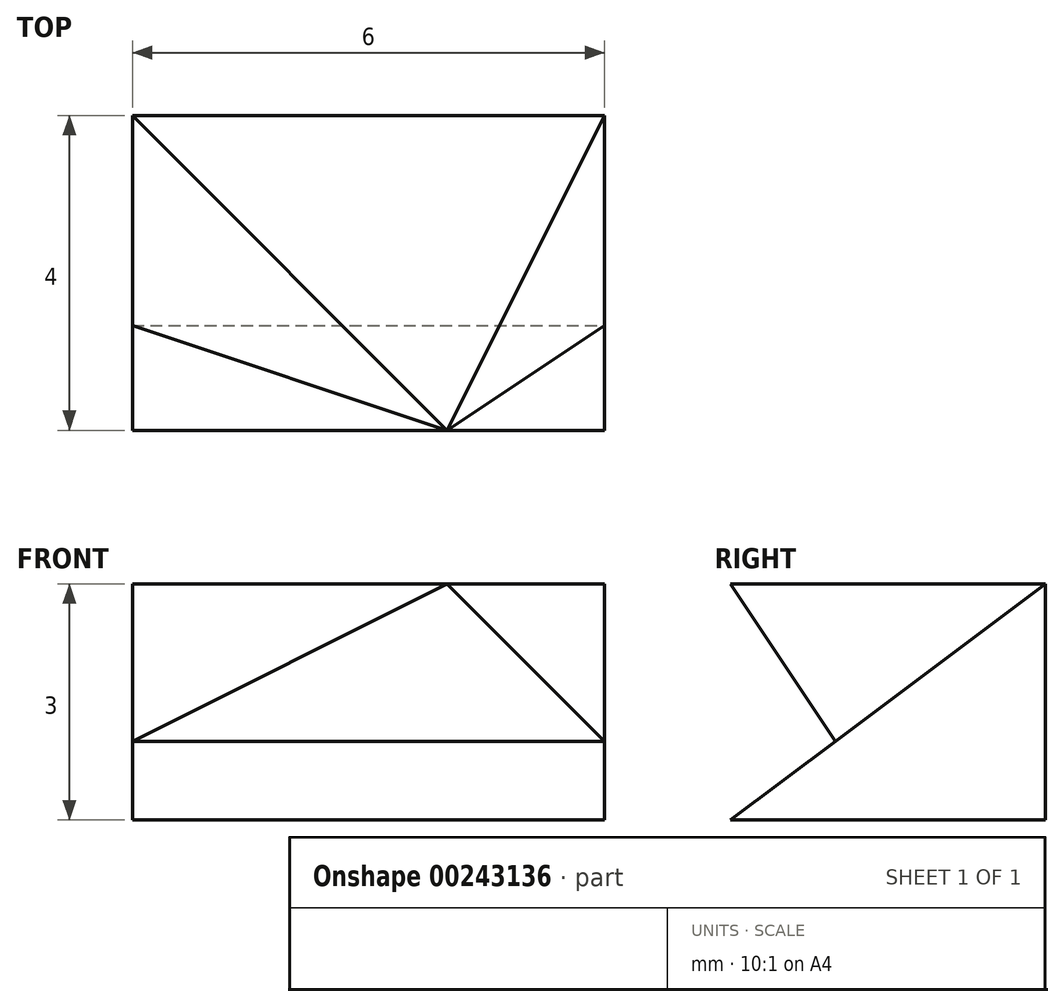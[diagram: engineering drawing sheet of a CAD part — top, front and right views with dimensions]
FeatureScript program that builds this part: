
annotation { "Feature Type Name" : "Feature", "Feature Type Description" : "" }
export const myFeature = defineFeature(function(context is Context, id is Id, definition is map)
    precondition{}
    {
        {
            var Q0;
            Q0=qCreatedBy(makeId("Top.planeOp"),FACE);
            var sketch = newSketch(context, id + "F0", { "sketchPlane" : qUnion([Q0])});
            skLineSegment(sketch, "E0.bottom", {"start": v(0, 0) * mm, "end": v(6, 0) * mm});
            skLineSegment(sketch, "E0.top", {"start": v(0, 4) * mm, "end": v(6, 4) * mm});
            skLineSegment(sketch, "E0.left", {"start": v(0, 0) * mm, "end": v(0, 4) * mm});
            skLineSegment(sketch, "E0.right", {"start": v(6, 0) * mm, "end": v(6, 4) * mm});
            skSolve(sketch);
        }
        {
            var Q0;
            Q0 = qSketchRegion(id + "F0", true);
            extrude(context, id + "F1", {"entities" : qUnion([Q0]), "depth" : 3 * mm});
        }
        {
            var Q0;
            Q0=makeQuery(id+"F1.opExtrude","SWEPT_FACE",FACE,{"disambiguationData":[OSD([sQuery(id+"F0.wireOp",EDGE,"E0.right")])]});
            var sketch = newSketch(context, id + "F2", { "sketchPlane" : qUnion([Q0])});
            skLineSegment(sketch, "E1", {"start": v(0, 0) * mm, "end": v(0, 3) * mm});
            skLineSegment(sketch, "E2", {"start": v(0, 3) * mm, "end": v(0, 0) * mm});
            skLineSegment(sketch, "E3", {"start": v(0, 3) * mm, "end": v(1.33, 1) * mm});
            skLineSegment(sketch, "E4", {"start": v(1.33, 1) * mm, "end": v(0, 0) * mm});
            skSolve(sketch);
        }
        {
            var Q0;
            Q0 = qSketchRegion(id + "F2", true);
            extrude(context, id + "F3", {"entities" : qUnion([Q0]), "operationType" : NewBodyOperationType.REMOVE, "oppositeDirection" : true, "depth" : 6 * mm});
        }
        {
            var Q0;
            Q0=makeQuery(id+"F1.opExtrude","CAP_FACE",FACE,{"disambiguationData":[OSD([sQuery(id+"F0.wireOp",EDGE,"E0.bottom"),sQuery(id+"F0.wireOp",EDGE,"E0.top"),sQuery(id+"F0.wireOp",EDGE,"E0.left"),sQuery(id+"F0.wireOp",EDGE,"E0.right")])],"isStart":false});
            var sketch = newSketch(context, id + "F4", { "sketchPlane" : qUnion([Q0])});
            skLineSegment(sketch, "E5", {"start": v(6, 4) * mm, "end": v(4, 4) * mm, "construction": true});
            skLineSegment(sketch, "E6", {"start": v(4, 4) * mm, "end": v(4, 0) * mm, "construction": true});
            skSolve(sketch);
        }
        {
            var Q0;
            Q0=makeQuery(id+"F1.opExtrude","CAP_VERTEX",VERTEX,{"disambiguationData":[OSD([sQuery(id+"F0.wireOp",EDGE,"E0.top"),sQuery(id+"F0.wireOp",EDGE,"E0.left")])],"isStart":false});
            var Q1;
            Q1=sQuery(id+"F4.wireOp",VERTEX,"E6.end");
            var Q2;
            Q2=makeQuery(id+"F3.boolean.opBoolean","COPY",VERTEX,{"derivedFrom":makeQuery(id+"F3.opExtrude","CAP_VERTEX",VERTEX,{"disambiguationData":[OSD([sQuery(id+"F2.wireOp",EDGE,"E3"),sQuery(id+"F2.wireOp",EDGE,"E4")])],"isStart":false})});
            cPlane(context, id + "F5", {"entities" : qUnion([Q0, Q1, Q2]), "cplaneType" : CPlaneType.THREE_POINT, "offset" : 25 * mm, "width" : 150 * mm, "height" : 150 * mm});
        }
        {
            var Q0;
            Q0=qCreatedBy(id+"F5.planeOp",FACE);
            var sketch = newSketch(context, id + "F6", { "sketchPlane" : qUnion([Q0])});
            skLineSegment(sketch, "E7", {"start": v(-4.64, 5.81) * mm, "end": v(9.84, 6.53) * mm});
            skLineSegment(sketch, "E8", {"start": v(9.84, 6.53) * mm, "end": v(8.06, -1.53) * mm});
            skLineSegment(sketch, "E9", {"start": v(8.06, -1.53) * mm, "end": v(-5.5, -1.53) * mm});
            skLineSegment(sketch, "E10", {"start": v(-5.5, -1.53) * mm, "end": v(-4.64, 5.81) * mm});
            skSolve(sketch);
        }
        {
            var Q0;
            Q0 = qSketchRegion(id + "F6", true);
            extrude(context, id + "F7", {"entities" : qUnion([Q0]), "operationType" : NewBodyOperationType.REMOVE, "depth" : 25 * mm});
        }
        {
            var Q0;
            Q0=sQuery(id+"F4.wireOp",VERTEX,"E6.end");
            var Q1;
            Q1=sQuery(id+"F4.wireOp",VERTEX,"E5.start");
            var Q2;
            Q2=makeQuery(id+"F3.boolean.opBoolean","COPY",VERTEX,{"derivedFrom":makeQuery(id+"F3.opExtrude","CAP_VERTEX",VERTEX,{"disambiguationData":[OSD([sQuery(id+"F2.wireOp",EDGE,"E3"),sQuery(id+"F2.wireOp",EDGE,"E4")])],"isStart":true})});
            cPlane(context, id + "F8", {"entities" : qUnion([Q0, Q1, Q2]), "cplaneType" : CPlaneType.THREE_POINT, "offset" : 25 * mm, "width" : 150 * mm, "height" : 150 * mm});
        }
        {
            var Q0;
            Q0=qCreatedBy(id+"F8.planeOp",FACE);
            var sketch = newSketch(context, id + "F9", { "sketchPlane" : qUnion([Q0])});
            skLineSegment(sketch, "E11", {"start": v(-0.44, 3.92) * mm, "end": v(12.37, -1.9) * mm});
            skLineSegment(sketch, "E12", {"start": v(12.37, -1.9) * mm, "end": v(9.87, -6.32) * mm});
            skLineSegment(sketch, "E13", {"start": v(9.87, -6.32) * mm, "end": v(-3.6, -2.35) * mm});
            skLineSegment(sketch, "E14", {"start": v(-3.6, -2.35) * mm, "end": v(-0.44, 3.92) * mm});
            skSolve(sketch);
        }
        {
            var Q0;
            Q0 = qSketchRegion(id + "F9", true);
            extrude(context, id + "F10", {"entities" : qUnion([Q0]), "operationType" : NewBodyOperationType.REMOVE, "depth" : 25 * mm});
        }
    });
